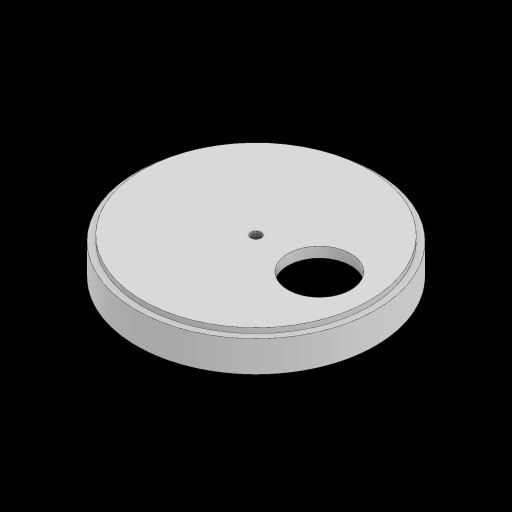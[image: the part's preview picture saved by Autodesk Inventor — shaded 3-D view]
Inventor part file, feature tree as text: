
AUTODESK INVENTOR PART (.ipt)
format: ipt  version: 2023 (Build 270158000, 158)  size: 132,608 bytes
history: native  units: in
note: dims shown in document units (in); Inventor stores cm internally (conversion verified against a paired STEP export)
features: extrude x3, sketch x3
ambient origin geometry x8: Origin, YZ Plane, XZ Plane, XY Plane, X Axis, Y Axis, Z Axis, Center Point
bodies: Solid1 (feature_tree)
feature tree (6):
  extrude  "Extrusion1"  Depth=0.25in
  extrude  "Extrusion2"  Depth=0.5in
  extrude  "Extrusion3"  Depth=0.75in
  sketch  "Sketch1"  dims[d1=1.5748in d2=5.125in d3=1.525in d4=1.5375in d5=360.0deg d6=0.25in d7=5.5in]
  sketch  "Sketch2"  dims[d8=0.5in d9=0.0in d10=5.3125in]
  sketch  "Sketch3"  dims[d11=0.25in d12=0.0in d13=5.8in d14=0.75in d15=0.0in]
